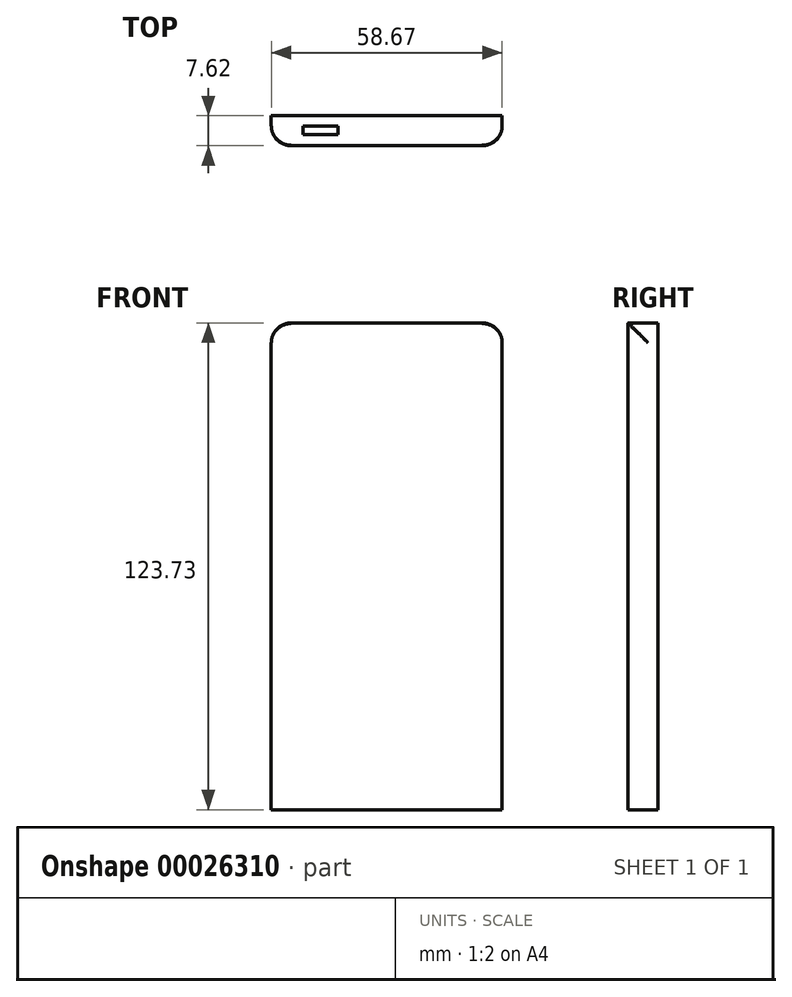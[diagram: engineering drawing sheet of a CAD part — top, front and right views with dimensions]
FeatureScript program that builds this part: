
annotation { "Feature Type Name" : "Feature", "Feature Type Description" : "" }
export const myFeature = defineFeature(function(context is Context, id is Id, definition is map)
    precondition{}
    {
        {
            var Q0;
            Q0=qCreatedBy(makeId("Front.planeOp"),FACE);
            var sketch = newSketch(context, id + "F0", { "sketchPlane" : qUnion([Q0])});
            skLineSegment(sketch, "E0.bottom", {"start": v(-37.9, 50.87) * mm, "end": v(20.77, 50.87) * mm});
            skLineSegment(sketch, "E0.top", {"start": v(-37.9, -72.83) * mm, "end": v(20.77, -72.83) * mm});
            skLineSegment(sketch, "E0.left", {"start": v(-37.9, 50.87) * mm, "end": v(-37.9, -72.83) * mm});
            skLineSegment(sketch, "E0.right", {"start": v(20.77, 50.87) * mm, "end": v(20.77, -72.83) * mm});
            skSolve(sketch);
        }
        {
            var Q0;
            Q0 = qSketchRegion(id + "F0", true);
            extrude(context, id + "F1", {"entities" : qUnion([Q0]), "depth" : 7.62 * mm});
        }
        {
            var Q0;
            Q0=makeQuery(id+"F1.opExtrude","CAP_EDGE",EDGE,{"disambiguationData":[OSD([sQuery(id+"F0.wireOp",EDGE,"E0.bottom")])],"isStart":false});
            fillet(context, id + "F2", {"entities" : qUnion([Q0]), "radius" : 0.13 * mm, "tangentPropagation" : true, "allowEdgeOverflow" : false});
        }
        {
            var Q0;
            Q0=makeQuery(id+"F1.opExtrude","SWEPT_EDGE",EDGE,{"disambiguationData":[OSD([sQuery(id+"F0.wireOp",EDGE,"E0.bottom"),sQuery(id+"F0.wireOp",EDGE,"E0.left")])]});
            fillet(context, id + "F3", {"entities" : qUnion([Q0]), "radius" : 5.08 * mm, "tangentPropagation" : true, "allowEdgeOverflow" : false});
        }
        {
            var Q0;
            Q0=makeQuery(id+"F1.opExtrude","SWEPT_EDGE",EDGE,{"disambiguationData":[OSD([sQuery(id+"F0.wireOp",EDGE,"E0.bottom"),sQuery(id+"F0.wireOp",EDGE,"E0.right")])]});
            fillet(context, id + "F4", {"entities" : qUnion([Q0]), "radius" : 5.08 * mm, "tangentPropagation" : true, "allowEdgeOverflow" : false});
        }
        {
            var Q0;
            Q0=makeQuery(id+"F1.opExtrude","SWEPT_FACE",FACE,{"disambiguationData":[OSD([sQuery(id+"F0.wireOp",EDGE,"E0.bottom")])]});
            var sketch = newSketch(context, id + "F5", { "sketchPlane" : qUnion([Q0])});
            skLineSegment(sketch, "E1.bottom", {"start": v(-29.78, -2.6) * mm, "end": v(-21, -2.6) * mm});
            skLineSegment(sketch, "E1.top", {"start": v(-29.78, -4.8) * mm, "end": v(-21, -4.8) * mm});
            skLineSegment(sketch, "E1.left", {"start": v(-29.78, -2.6) * mm, "end": v(-29.78, -4.8) * mm});
            skLineSegment(sketch, "E1.right", {"start": v(-21, -2.6) * mm, "end": v(-21, -4.8) * mm});
            skSolve(sketch);
        }
        {
            var Q0;
            Q0 = qSketchRegion(id + "F5", true);
            extrude(context, id + "F6", {"entities" : qUnion([Q0]), "operationType" : NewBodyOperationType.ADD, "depth" : 0.03 * mm});
        }
    });
